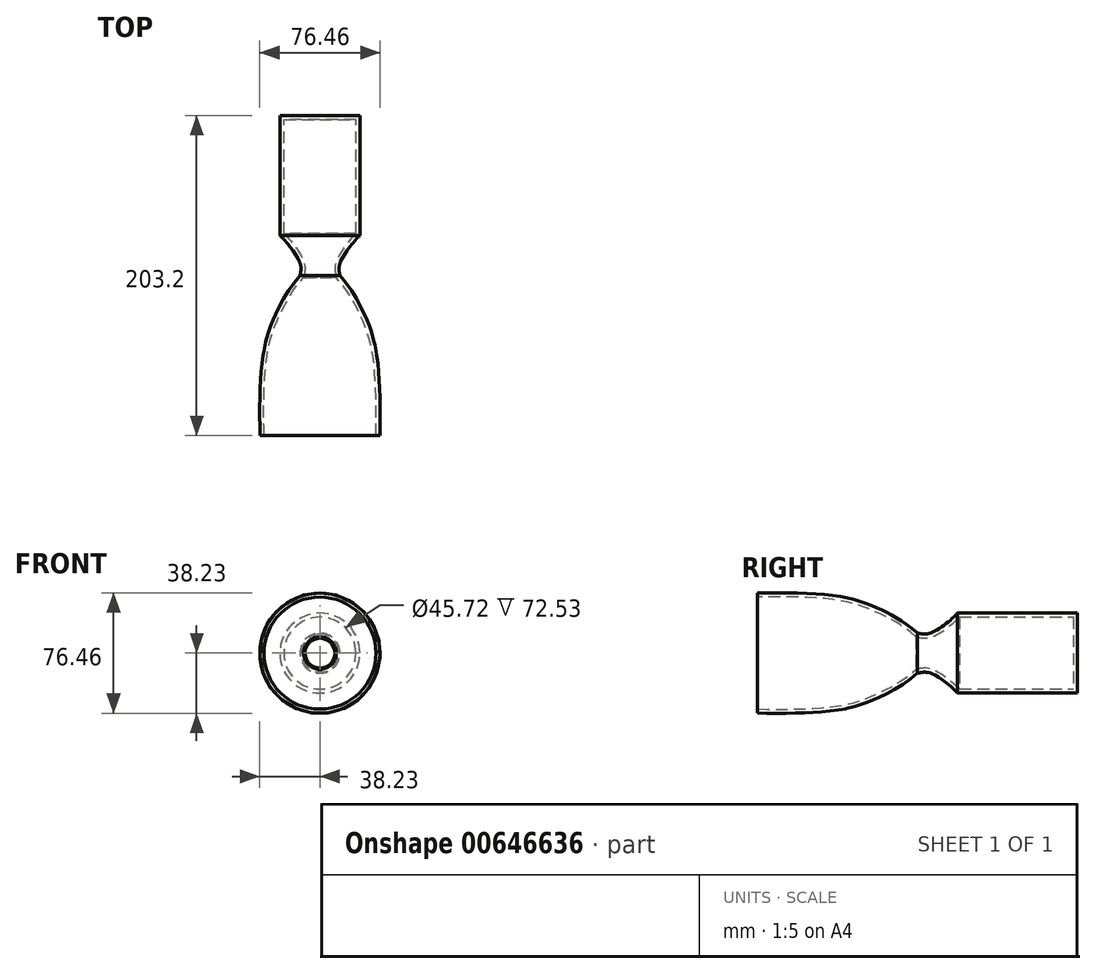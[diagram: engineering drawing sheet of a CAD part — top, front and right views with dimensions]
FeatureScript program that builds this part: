
annotation { "Feature Type Name" : "Feature", "Feature Type Description" : "" }
export const myFeature = defineFeature(function(context is Context, id is Id, definition is map)
    precondition{}
    {
        {
            var Q0;
            Q0=qCreatedBy(makeId("Right.planeOp"),FACE);
            var sketch = newSketch(context, id + "F0", { "sketchPlane" : qUnion([Q0])});
            skLineSegment(sketch, "E0.bottom", {"start": v(0, 0) * mm, "end": v(-101.6, 0) * mm});
            skLineSegment(sketch, "E1", {"start": v(0, 0) * mm, "end": v(0, 12.7) * mm});
            skLineSegment(sketch, "E2", {"start": v(-101.6, 0) * mm, "end": v(-101.6, 38.1) * mm});
            skFitSpline(sketch, "E3", {"points": [v(0, 12.7) * mm, v(-21.54, 26.7) * mm, v(-45.6, 35.22) * mm, v(-101.6, 38.1) * mm], "startDerivative": vector(-85.2, 74.56) * mm, "endDerivative": vector(-152.88, -2.68) * mm});
            skLineSegment(sketch, "E4.bottom", {"start": v(25.4, 0) * mm, "end": v(101.6, 0) * mm});
            skLineSegment(sketch, "E4.top", {"start": v(25.4, 25.4) * mm, "end": v(101.6, 25.4) * mm});
            skLineSegment(sketch, "E4.left", {"start": v(25.4, 0) * mm, "end": v(25.4, 25.4) * mm});
            skLineSegment(sketch, "E4.right", {"start": v(101.6, 0) * mm, "end": v(101.6, 25.4) * mm});
            skFitSpline(sketch, "E5", {"points": [v(0, 12.7) * mm, v(8.06, 12.7) * mm, v(25.4, 25.4) * mm], "startDerivative": vector(17.59, -2.91) * mm, "endDerivative": vector(12.96, 15.35) * mm});
            skLineSegment(sketch, "E6", {"start": v(0, 0) * mm, "end": v(25.4, 0) * mm});
            skSolve(sketch);
        }
        {
            var Q0;
            Q0=makeQuery(id+"F0.imprint","IMPRINT",FACE,{"disambiguationData":[TD([[makeQuery(id+"F0.imprint","IMPRINT",EDGE,{"derivedFrom":sQuery(id+"F0.wireOp",EDGE,"E0.bottom")}),-1.0]])]});
            var Q1;
            Q1=makeQuery(id+"F0.imprint","IMPRINT",FACE,{"disambiguationData":[TD([[makeQuery(id+"F0.imprint","IMPRINT",EDGE,{"derivedFrom":sQuery(id+"F0.wireOp",EDGE,"E1")}),-1.0]])]});
            var Q2;
            Q2=makeQuery(id+"F0.imprint","IMPRINT",FACE,{"disambiguationData":[TD([[makeQuery(id+"F0.imprint","IMPRINT",EDGE,{"derivedFrom":sQuery(id+"F0.wireOp",EDGE,"E4.bottom")}),1.0]])]});
            var Q3;
            Q3=sQuery(id+"F0.wireOp",EDGE,"E0.bottom");
            revolve(context, id + "F1", {"entities" : qUnion([Q0, Q1, Q2]), "axis" : qUnion([Q3]), "revolveType" : RevolveType.FULL});
        }
        {
            var Q0;
            Q0=makeQuery(id+"F1.opRevolve","SWEPT_FACE",FACE,{"disambiguationData":[OSD([sQuery(id+"F0.wireOp",EDGE,"E2")])]});
            shell(context, id + "F2", {"entities" : qUnion([Q0]), "thickness" : 2.54 * mm});
        }
    });
